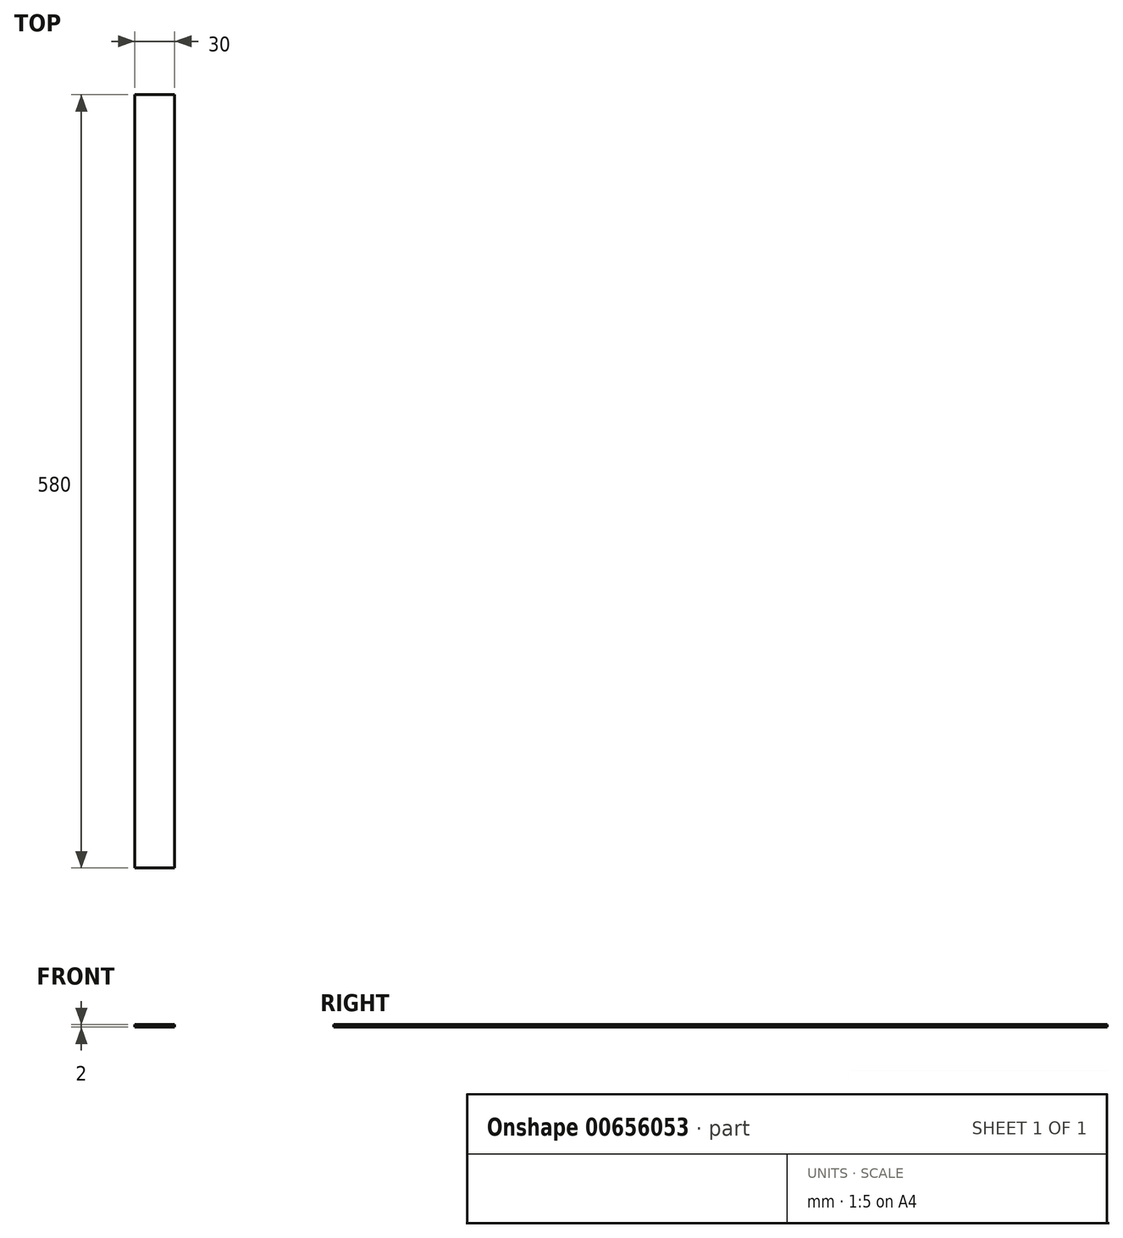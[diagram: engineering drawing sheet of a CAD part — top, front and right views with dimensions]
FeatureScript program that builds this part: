
annotation { "Feature Type Name" : "Feature", "Feature Type Description" : "" }
export const myFeature = defineFeature(function(context is Context, id is Id, definition is map)
    precondition{}
    {
        {
            var Q0;
            Q0=qCreatedBy(makeId("Front.planeOp"),FACE);
            var sketch = newSketch(context, id + "F0", { "sketchPlane" : qUnion([Q0])});
            skLineSegment(sketch, "E0", {"start": v(15, 2) * mm, "end": v(15, 0) * mm});
            skLineSegment(sketch, "E1", {"start": v(15, 0) * mm, "end": v(0, 0) * mm});
            skLineSegment(sketch, "E2", {"start": v(0, 0) * mm, "end": v(0, 30) * mm, "construction": true});
            skLineSegment(sketch, "E3.MirrorCS", {"start": v(-15, 2) * mm, "end": v(-15, 0) * mm});
            skLineSegment(sketch, "E4.MirrorCS", {"start": v(-15, 0) * mm, "end": v(0, 0) * mm});
            skLineSegment(sketch, "E5", {"start": v(15, 2) * mm, "end": v(-15, 2) * mm});
            skSolve(sketch);
        }
        {
            var Q0;
            Q0=makeQuery(id+"F0.imprint","IMPRINT",FACE,{"disambiguationData":[TD([[makeQuery(id+"F0.imprint","IMPRINT",EDGE,{"derivedFrom":sQuery(id+"F0.wireOp",EDGE,"E0")}),-1.0]])]});
            extrude(context, id + "F1", {"entities" : qUnion([Q0]), "depth" : 580 * mm, "offsetDistance" : 25.4 * mm});
        }
    });
